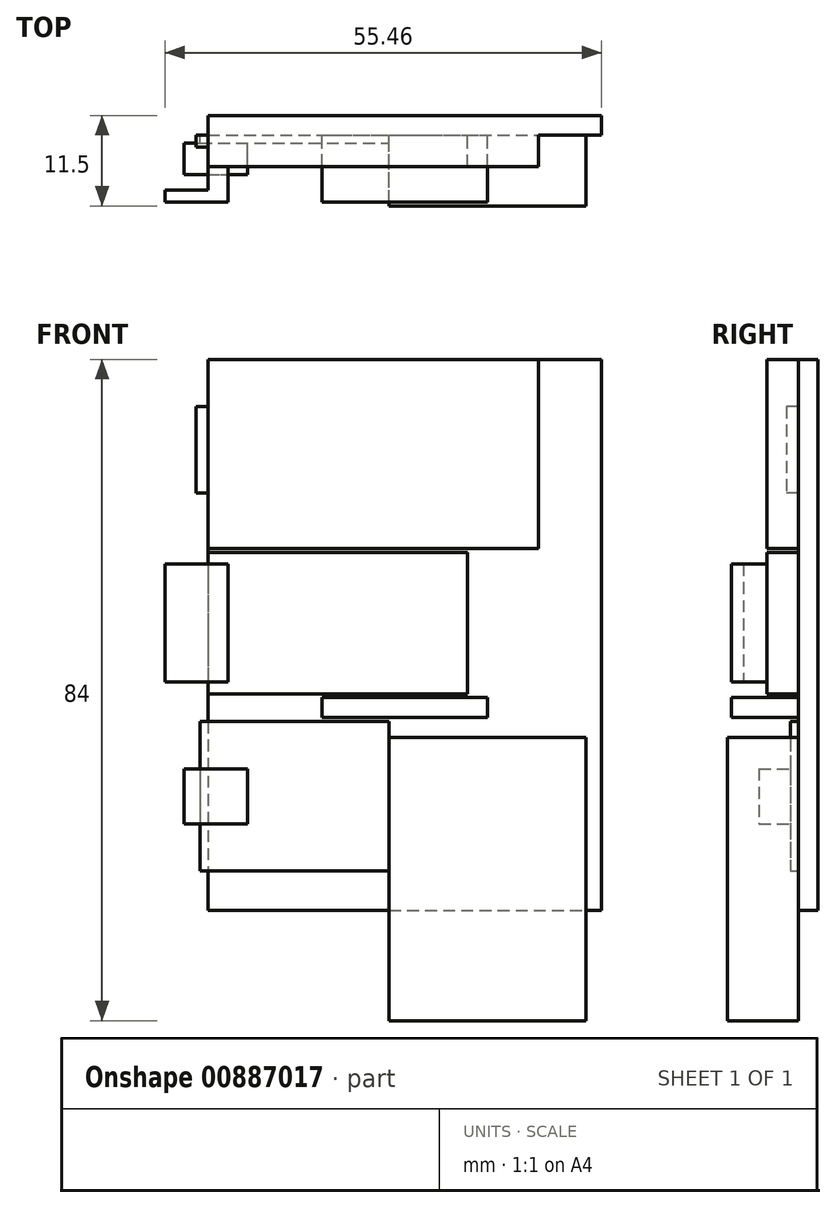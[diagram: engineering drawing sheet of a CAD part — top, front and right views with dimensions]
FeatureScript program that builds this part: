
annotation { "Feature Type Name" : "Feature", "Feature Type Description" : "" }
export const myFeature = defineFeature(function(context is Context, id is Id, definition is map)
    precondition{}
    {
        {
            var Q0;
            Q0=qCreatedBy(makeId("Front.planeOp"),FACE);
            var sketch = newSketch(context, id + "F0", { "sketchPlane" : qUnion([Q0])});
            skLineSegment(sketch, "E0.bottom", {"start": v(-25, 35) * mm, "end": v(25, 35) * mm});
            skLineSegment(sketch, "E0.top", {"start": v(-25, -35) * mm, "end": v(25, -35) * mm});
            skLineSegment(sketch, "E0.left", {"start": v(-25, 35) * mm, "end": v(-25, -35) * mm});
            skLineSegment(sketch, "E0.right", {"start": v(25, 35) * mm, "end": v(25, -35) * mm});
            skSolve(sketch);
        }
        {
            var Q0;
            Q0 = qSketchRegion(id + "F0", true);
            extrude(context, id + "F1", {"entities" : qUnion([Q0]), "depth" : 1 * mm, "offsetDistance" : 25 * mm});
        }
        {
            var Q0;
            Q0=makeQuery(id+"F1.opExtrude","CAP_FACE",FACE,{"disambiguationData":[OSD([sQuery(id+"F0.wireOp",EDGE,"E0.bottom"),sQuery(id+"F0.wireOp",EDGE,"E0.top"),sQuery(id+"F0.wireOp",EDGE,"E0.left"),sQuery(id+"F0.wireOp",EDGE,"E0.right")])],"isStart":false});
            var sketch = newSketch(context, id + "F2", { "sketchPlane" : qUnion([Q0])});
            skLineSegment(sketch, "E1.bottom", {"start": v(-25, 35) * mm, "end": v(17, 35) * mm});
            skLineSegment(sketch, "E1.top", {"start": v(-25, 11) * mm, "end": v(17, 11) * mm});
            skLineSegment(sketch, "E1.left", {"start": v(-25, 35) * mm, "end": v(-25, 11) * mm});
            skLineSegment(sketch, "E1.right", {"start": v(17, 35) * mm, "end": v(17, 11) * mm});
            skSolve(sketch);
        }
        {
            var Q0;
            Q0 = qSketchRegion(id + "F2", true);
            extrude(context, id + "F3", {"entities" : qUnion([Q0]), "operationType" : NewBodyOperationType.ADD, "depth" : 4 * mm, "offsetDistance" : 25 * mm});
        }
        {
            var Q0;
            Q0=makeQuery(id+"F1.opExtrude","CAP_FACE",FACE,{"disambiguationData":[OSD([sQuery(id+"F0.wireOp",EDGE,"E0.bottom"),sQuery(id+"F0.wireOp",EDGE,"E0.top"),sQuery(id+"F0.wireOp",EDGE,"E0.left"),sQuery(id+"F0.wireOp",EDGE,"E0.right")])],"isStart":false});
            var sketch = newSketch(context, id + "F4", { "sketchPlane" : qUnion([Q0])});
            skLineSegment(sketch, "E2.bottom", {"start": v(-2, -13) * mm, "end": v(23, -13) * mm});
            skLineSegment(sketch, "E2.top", {"start": v(-2, -49) * mm, "end": v(23, -49) * mm});
            skLineSegment(sketch, "E2.left", {"start": v(-2, -13) * mm, "end": v(-2, -49) * mm});
            skLineSegment(sketch, "E2.right", {"start": v(23, -13) * mm, "end": v(23, -49) * mm});
            skSolve(sketch);
        }
        {
            var Q0;
            Q0 = qSketchRegion(id + "F4", true);
            extrude(context, id + "F5", {"entities" : qUnion([Q0]), "operationType" : NewBodyOperationType.ADD, "depth" : 9 * mm, "offsetDistance" : 25 * mm});
        }
        {
            var Q0;
            Q0=makeQuery(id+"F1.opExtrude","CAP_FACE",FACE,{"disambiguationData":[OSD([sQuery(id+"F0.wireOp",EDGE,"E0.bottom"),sQuery(id+"F0.wireOp",EDGE,"E0.top"),sQuery(id+"F0.wireOp",EDGE,"E0.left"),sQuery(id+"F0.wireOp",EDGE,"E0.right")])],"isStart":false});
            var sketch = newSketch(context, id + "F6", { "sketchPlane" : qUnion([Q0])});
            skLineSegment(sketch, "E3.bottom", {"start": v(-26, -11) * mm, "end": v(-2, -11) * mm});
            skLineSegment(sketch, "E3.top", {"start": v(-26, -30) * mm, "end": v(-2, -30) * mm});
            skLineSegment(sketch, "E3.left", {"start": v(-26, -11) * mm, "end": v(-26, -30) * mm});
            skLineSegment(sketch, "E3.right", {"start": v(-2, -11) * mm, "end": v(-2, -30) * mm});
            skSolve(sketch);
        }
        {
            var Q0;
            Q0 = qSketchRegion(id + "F6", true);
            extrude(context, id + "F7", {"entities" : qUnion([Q0]), "operationType" : NewBodyOperationType.ADD, "depth" : 1 * mm, "offsetDistance" : 25 * mm});
        }
        {
            var Q0;
            Q0=makeQuery(id+"F7.opExtrude","CAP_FACE",FACE,{"disambiguationData":[OSD([sQuery(id+"F6.wireOp",EDGE,"E3.bottom"),sQuery(id+"F6.wireOp",EDGE,"E3.top"),sQuery(id+"F6.wireOp",EDGE,"E3.left"),sQuery(id+"F6.wireOp",EDGE,"E3.right")])],"isStart":false});
            var sketch = newSketch(context, id + "F8", { "sketchPlane" : qUnion([Q0])});
            skLineSegment(sketch, "E4", {"start": v(-31.05, -20.5) * mm, "end": v(21.16, -20.5) * mm, "construction": true});
            skLineSegment(sketch, "E5.bottom", {"start": v(-28, -17) * mm, "end": v(-20, -17) * mm});
            skLineSegment(sketch, "E5.top", {"start": v(-28, -24) * mm, "end": v(-20, -24) * mm});
            skLineSegment(sketch, "E5.left", {"start": v(-28, -17) * mm, "end": v(-28, -24) * mm});
            skLineSegment(sketch, "E5.right", {"start": v(-20, -17) * mm, "end": v(-20, -24) * mm});
            skSolve(sketch);
        }
        {
            var Q0;
            Q0 = qSketchRegion(id + "F8", true);
            extrude(context, id + "F9", {"entities" : qUnion([Q0]), "operationType" : NewBodyOperationType.ADD, "depth" : 4 * mm, "offsetDistance" : 25 * mm});
        }
        {
            var Q0;
            {var subQ4=sQuery(id+"F0.wireOp",EDGE,"E0.left");var subQ5=sQuery(id+"F0.wireOp",EDGE,"E0.bottom");var subQ6=sQuery(id+"F0.wireOp",EDGE,"E0.right");var subQ7=sQuery(id+"F0.wireOp",EDGE,"E0.top");Q0=makeQuery(id+"F7.boolean.opBoolean","SPLIT",FACE,{"disambiguationData":[TD([makeQuery(id+"F1.opExtrude","SWEPT_FACE",FACE,{"disambiguationData":[OSD([subQ5])]})])],"derivedFrom":makeQuery(id+"F1.opExtrude","CAP_FACE",FACE,{"disambiguationData":[OSD([subQ5,subQ7,subQ4,subQ6])],"isStart":false})});}
            var sketch = newSketch(context, id + "F10", { "sketchPlane" : qUnion([Q0])});
            skLineSegment(sketch, "E6.bottom", {"start": v(-25, 10.5) * mm, "end": v(8, 10.5) * mm});
            skLineSegment(sketch, "E6.top", {"start": v(-25, -7.5) * mm, "end": v(8, -7.5) * mm});
            skLineSegment(sketch, "E6.left", {"start": v(-25, 10.5) * mm, "end": v(-25, -7.5) * mm});
            skLineSegment(sketch, "E6.right", {"start": v(8, 10.5) * mm, "end": v(8, -7.5) * mm});
            skSolve(sketch);
        }
        {
            var Q0;
            Q0 = qSketchRegion(id + "F10", true);
            extrude(context, id + "F11", {"entities" : qUnion([Q0]), "operationType" : NewBodyOperationType.ADD, "depth" : 4 * mm, "offsetDistance" : 25 * mm});
        }
        {
            var Q0;
            Q0=makeQuery(id+"F11.opExtrude","CAP_FACE",FACE,{"disambiguationData":[OSD([sQuery(id+"F10.wireOp",EDGE,"E6.bottom"),sQuery(id+"F10.wireOp",EDGE,"E6.top"),sQuery(id+"F10.wireOp",EDGE,"E6.left"),sQuery(id+"F10.wireOp",EDGE,"E6.right")])],"isStart":false});
            var sketch = newSketch(context, id + "F12", { "sketchPlane" : qUnion([Q0])});
            skLineSegment(sketch, "E7", {"start": v(-28.01, 1.5) * mm, "end": v(21.47, 1.5) * mm, "construction": true});
            skLineSegment(sketch, "E8.bottom", {"start": v(-25, 9) * mm, "end": v(-22.46, 9) * mm});
            skLineSegment(sketch, "E8.top", {"start": v(-25, -6) * mm, "end": v(-22.46, -6) * mm});
            skLineSegment(sketch, "E8.left", {"start": v(-25, 9) * mm, "end": v(-25, -6) * mm});
            skLineSegment(sketch, "E8.right", {"start": v(-22.46, 9) * mm, "end": v(-22.46, -6) * mm});
            skSolve(sketch);
        }
        {
            var Q0;
            Q0 = qSketchRegion(id + "F12", true);
            extrude(context, id + "F13", {"entities" : qUnion([Q0]), "operationType" : NewBodyOperationType.ADD, "depth" : 3 * mm, "offsetDistance" : 25 * mm});
        }
        {
            var Q0;
            Q0=makeQuery(id+"F13.opExtrude","SWEPT_FACE",FACE,{"disambiguationData":[OSD([sQuery(id+"F12.wireOp",EDGE,"E8.top")])]});
            var sketch = newSketch(context, id + "F14", { "sketchPlane" : qUnion([Q0])});
            skLineSegment(sketch, "E9.bottom", {"start": v(-30.46, 9.5) * mm, "end": v(-22.46, 9.5) * mm});
            skLineSegment(sketch, "E9.top", {"start": v(-30.46, 8) * mm, "end": v(-22.46, 8) * mm});
            skLineSegment(sketch, "E9.left", {"start": v(-30.46, 9.5) * mm, "end": v(-30.46, 8) * mm});
            skLineSegment(sketch, "E9.right", {"start": v(-22.46, 9.5) * mm, "end": v(-22.46, 8) * mm});
            skSolve(sketch);
        }
        {
            var Q0;
            Q0=makeQuery(id+"F14.imprint","IMPRINT",FACE,{"disambiguationData":[TD([[makeQuery(id+"F14.imprint","IMPRINT",EDGE,{"derivedFrom":sQuery(id+"F14.wireOp",EDGE,"E9.bottom")}),-1.0]])]});
            var Q1;
            Q1=makeQuery(id+"F13.opExtrude","SWEPT_FACE",FACE,{"disambiguationData":[OSD([sQuery(id+"F12.wireOp",EDGE,"E8.bottom")])]});
            extrude(context, id + "F15", {"entities" : qUnion([Q0]), "operationType" : NewBodyOperationType.ADD, "endBound" : BoundingType.UP_TO_SURFACE, "oppositeDirection" : true, "depth" : 25 * mm, "endBoundEntityFace" : qUnion([Q1]), "offsetDistance" : 25 * mm});
        }
        {
            var Q0;
            {var subQ4=sQuery(id+"F0.wireOp",EDGE,"E0.left");var subQ5=sQuery(id+"F0.wireOp",EDGE,"E0.bottom");var subQ6=sQuery(id+"F0.wireOp",EDGE,"E0.right");var subQ7=sQuery(id+"F0.wireOp",EDGE,"E0.top");Q0=makeQuery(id+"F7.boolean.opBoolean","SPLIT",FACE,{"disambiguationData":[TD([makeQuery(id+"F1.opExtrude","SWEPT_FACE",FACE,{"disambiguationData":[OSD([subQ5])]})])],"derivedFrom":makeQuery(id+"F1.opExtrude","CAP_FACE",FACE,{"disambiguationData":[OSD([subQ5,subQ7,subQ4,subQ6])],"isStart":false})});}
            var sketch = newSketch(context, id + "F16", { "sketchPlane" : qUnion([Q0])});
            skLineSegment(sketch, "E10", {"start": v(0, 67.82) * mm, "end": v(0, -85.53) * mm, "construction": true});
            skLineSegment(sketch, "E11.bottom", {"start": v(-10.5, -7.96) * mm, "end": v(10.5, -7.96) * mm});
            skLineSegment(sketch, "E11.top", {"start": v(-10.5, -10.5) * mm, "end": v(10.5, -10.5) * mm});
            skLineSegment(sketch, "E11.left", {"start": v(-10.5, -7.96) * mm, "end": v(-10.5, -10.5) * mm});
            skLineSegment(sketch, "E11.right", {"start": v(10.5, -7.96) * mm, "end": v(10.5, -10.5) * mm});
            skSolve(sketch);
        }
        {
            var Q0;
            Q0 = qSketchRegion(id + "F16", true);
            extrude(context, id + "F17", {"entities" : qUnion([Q0]), "operationType" : NewBodyOperationType.ADD, "depth" : 8.5 * mm, "offsetDistance" : 25 * mm});
        }
        {
            var Q0;
            Q0=makeQuery(id+"F13.boolean.opBoolean","MERGE",FACE,{"derivedFrom":[makeQuery(id+"F11.boolean.opBoolean","MERGE",FACE,{"derivedFrom":[makeQuery(id+"F3.boolean.opBoolean","MERGE",FACE,{"derivedFrom":[makeQuery(id+"F1.opExtrude","SWEPT_FACE",FACE,{"disambiguationData":[OSD([sQuery(id+"F0.wireOp",EDGE,"E0.left")])]}),makeQuery(id+"F3.opExtrude","SWEPT_FACE",FACE,{"disambiguationData":[OSD([sQuery(id+"F2.wireOp",EDGE,"E1.left")])]})]}),makeQuery(id+"F11.opExtrude","SWEPT_FACE",FACE,{"disambiguationData":[OSD([sQuery(id+"F10.wireOp",EDGE,"E6.left")])]})]}),makeQuery(id+"F13.opExtrude","SWEPT_FACE",FACE,{"disambiguationData":[OSD([sQuery(id+"F12.wireOp",EDGE,"E8.left")])]})]});
            var sketch = newSketch(context, id + "F18", { "sketchPlane" : qUnion([Q0])});
            skLineSegment(sketch, "E12.bottom", {"start": v(1, 29) * mm, "end": v(2.5, 29) * mm});
            skLineSegment(sketch, "E12.top", {"start": v(1, 18) * mm, "end": v(2.5, 18) * mm});
            skLineSegment(sketch, "E12.left", {"start": v(1, 29) * mm, "end": v(1, 18) * mm});
            skLineSegment(sketch, "E12.right", {"start": v(2.5, 29) * mm, "end": v(2.5, 18) * mm});
            skSolve(sketch);
        }
        {
            var Q0;
            Q0 = qSketchRegion(id + "F18", true);
            extrude(context, id + "F19", {"entities" : qUnion([Q0]), "operationType" : NewBodyOperationType.ADD, "depth" : 1.5 * mm, "offsetDistance" : 25 * mm});
        }
        {
            var Q0;
            Q0=makeQuery(id+"F1.opExtrude","CAP_FACE",FACE,{"disambiguationData":[OSD([sQuery(id+"F0.wireOp",EDGE,"E0.bottom"),sQuery(id+"F0.wireOp",EDGE,"E0.top"),sQuery(id+"F0.wireOp",EDGE,"E0.left"),sQuery(id+"F0.wireOp",EDGE,"E0.right")])],"isStart":true});
            extrude(context, id + "F20", {"entities" : qUnion([Q0]), "operationType" : NewBodyOperationType.ADD, "depth" : 1.5 * mm, "offsetDistance" : 25 * mm});
        }
    });
